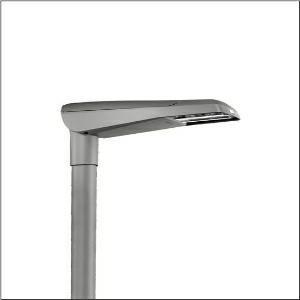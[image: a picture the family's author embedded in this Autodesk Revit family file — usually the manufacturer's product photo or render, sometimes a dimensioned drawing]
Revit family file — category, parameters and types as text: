
# Revit family: streetlight_sl_11_iq_micro___st1_2a_5xc1ac1f08ce_6c95
name_source: partatom
category: Lighting Fixtures
units: mm (PartAtom-declared; Revit-internal decimal feet)

## family parameters
Cut with Voids When Loaded = No
Host = Face
Light Source = No
Part Type = Normal
Room Calculation Point = No
Round Connector Dimension = Use Diameter
Shared = No

## types (1)
- --- (1 x LED, 1600 lm, 14 W, 2200K)
    Apparent Load = 14 VA
    CIE Flux Codes = 33 71 96 100 100
    Color Rendering = 70
    Color Temperature = 2200K
    Default Elevation = 1800 mm
    Description = Streetlight SL 11 iQ micro, mast luminaire, primary light control with 3 zone facetted reflector, of plastic, silver coated, highly specular, primary optical cover: cover, of PMMA, transparent, light distribution: ST1.2a, light emission: direct distribution, primary light characteristic: asymmetric, installation type: post-top, side-entry, lamps: LED, High Power LED, rated values: 1.880lm | 13,8W | 136,2lm/W (begin service life); end service life: 1.880lm | 14W; at 50% lumin. flux: 940lm | 7,5W | 125,3lm/W, colour temperature: 2200/2700/3000/4000K, colour rendering: CRI > 70, light colour: 722/727/730/740, light setting 1 begin service life: 100% | 1.880lm | 13,8W | 136,2lm/W | 3.000K, light setting 1 end service life: 14W, further light settings possible, control: Street-Remote, Auto-Match, Temp-Guard, Lumen-Switch, Night-Set, Smart-Wire, Light-Fading, Desk-Remote (wireless, voltage-free reading and setting of iQ features in the workshop via application-optimized NFC function/RFID function), optimised constant luminous flux control (CLO 2.0), with cable H07RN-F 3x 1.5mm², mains connection: 220..240V, AC, 50/60Hz, connection cable pre-assembled, cable length: 5,5m, luminaire housing, of diecast aluminium, powder-coated, SITECO metallic grey (DB 702S), please order mast flange separately, inclination adjustable without tools: 0°, 5°, 10°, 15° (post-top) | 0°, -5°, -10°, -15° (side-entry), sealing non-destructively replaceable, multi-level sealing system, length: 600mm, width: 174mm, height: 116mm, mast flange for spigot size: 42mm (side-entry): 5XC10008XM4, 60/48mm (side-entry/post-top): 5XC10108XM2, 76/60mm (side-entry/post-top): 5XC10108XM1, equipment: standard, protection rating (complete): IP66, insulation class (complete): insulation class II (safety insulation), certification: CE, ENEC, ENEC+, VDE, impact resistance: IK10, permissible operating ambient temperature for outdoor applications: -25..+50°C, standard-compliant lighting for roads and squares, Environmental Product Declaration (EPD) tested and certified by an independent institute, packaging unit: 1 piece

Light Distribution: ST1.2a
    Height = 116 mm
    Lamp = 1 x LED
    Lamp Light Flux = 1600 lm
    Lamp Power = 14 W
    Lamp count = 1
    Length = 600 mm
    Luminous efficacy = 114 lm/W
    Manufacturer = Siteco
    ModVariant = No
    Model = 5XC1AC1F08CE
    Number of Poles = 1
    OnlyDefault = Yes
    Power Factor = 1
    Product Name = Streetlight SL 11 iQ micro | ST1.2a
    Product group = mast luminaire | pylon top
    ProductGroupID = 6100
    Protection Class = Protection class II
    Protection Degree = IP 66
    RLX_Detail_Level = 1
    RLX_Emergency_Light_Flux = 0 lm
    RLX_Emergency_Type = 0
    RLX_Emergency_Type_DB = No
    RlxData = <blob elided: 58441 chars, md5=3266efce>
    Socket = socket
    Standby Power = 0 W
    System Light Flux = 1600 lm
    System Power = 14 W
    Type Comments = individual setting: luminous flux: 100 % | dim-lin: 254 | 369 mA
    Type Image = l_1006566.jpg
    URL = http://relux.com
    VarID = @adj_042267
    Voltage = 0 V
    Weight = 0.00 kg
    Width = 174 mm

## geometry (parser evidence)
native form markers: Blend x4, Sweep x11
no freeform markers — native parametric forms only
